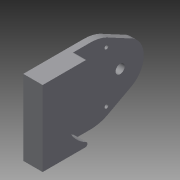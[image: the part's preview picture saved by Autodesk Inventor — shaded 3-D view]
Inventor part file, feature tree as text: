
AUTODESK INVENTOR PART (.ipt)
format: ipt  version: 2015 (Build 190159000, 159)  size: 110,080 bytes
history: native  units: mm
features: extrude x2, sketch x2, fillet x1
ambient origin geometry x8: Origin, YZ Plane, XZ Plane, XY Plane, X Axis, Y Axis, Z Axis, Center Point
bodies: Body1 (feature_tree)
feature tree (5):
  extrude  "Extrusion3"  Depth=8.5mm
  extrude  "Extrusion4"  Depth=2.0mm
  fillet  "Fillet1"  Radius=12.7mm
  sketch  "Sketch3"  dims[d4=32.0mm d9=50.0mm d27=44.0mm d28=44.0mm d31=8.5mm]
  sketch  "Sketch4"  dims[d32=44.0mm d33=27.64mm d35=12.7mm d36=23.82mm d37=23.82mm d38=3.5mm d40=3.5mm d41=84.0mm d42=18.0mm d43=0.0mm d44=27.64mm d45=12.0mm d46=0.0mm d47=2.0mm]
